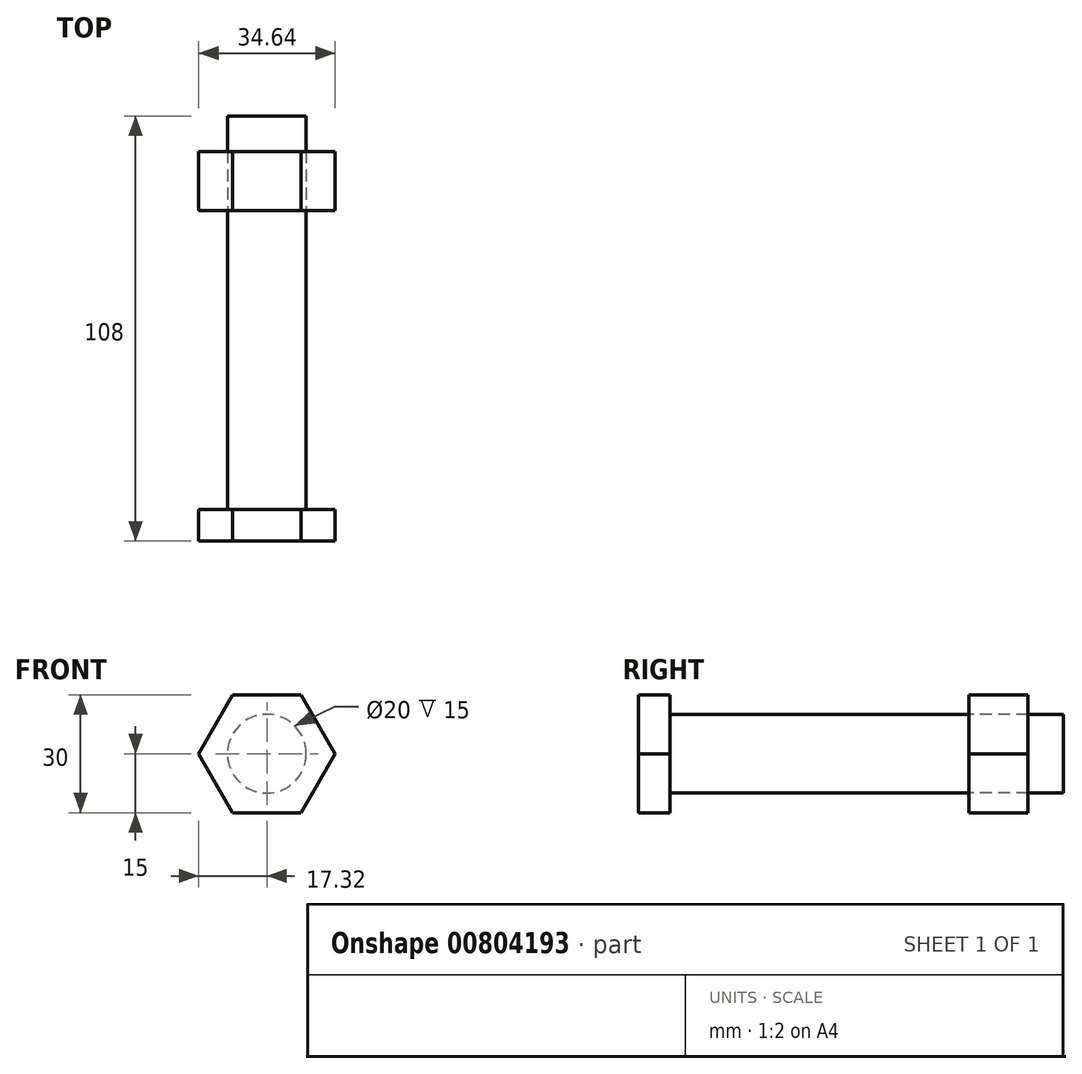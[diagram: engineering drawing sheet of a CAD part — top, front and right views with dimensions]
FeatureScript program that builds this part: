
annotation { "Feature Type Name" : "Feature", "Feature Type Description" : "" }
export const myFeature = defineFeature(function(context is Context, id is Id, definition is map)
    precondition{}
    {
        {
            var Q0;
            Q0=qCreatedBy(makeId("Front.planeOp"),FACE);
            var sketch = newSketch(context, id + "F0", { "sketchPlane" : qUnion([Q0])});
            skCircle(sketch, "E0.cCircle", {"center": v(0, 0) * mm, "radius": 15 * mm, "construction": true});
            skLineSegment(sketch, "E0.0", {"start": v(8.66, 15) * mm, "end": v(17.32, 0) * mm});
            skLineSegment(sketch, "E0.1", {"start": v(17.32, 0) * mm, "end": v(8.66, -15) * mm});
            skLineSegment(sketch, "E0.2", {"start": v(8.66, -15) * mm, "end": v(-8.66, -15) * mm});
            skLineSegment(sketch, "E0.3", {"start": v(-8.66, -15) * mm, "end": v(-17.32, 0) * mm});
            skLineSegment(sketch, "E0.4", {"start": v(-17.32, 0) * mm, "end": v(-8.66, 15) * mm});
            skLineSegment(sketch, "E0.5", {"start": v(-8.66, 15) * mm, "end": v(8.66, 15) * mm});
            skPoint(sketch, "E0.0.midPoint", {"position": v(13, 7.5) * mm});
            skLineSegment(sketch, "E1", {"start": v(0, 0) * mm, "end": v(0, 15) * mm, "construction": true});
            skSolve(sketch);
        }
        {
            var Q0;
            Q0 = qSketchRegion(id + "F0", true);
            extrude(context, id + "F1", {"entities" : qUnion([Q0]), "depth" : 8 * mm, "offsetDistance" : 25 * mm});
        }
        {
            var Q0;
            Q0=makeQuery(id+"F1.opExtrude","CAP_FACE",FACE,{"disambiguationData":[OSD([sQuery(id+"F0.wireOp",EDGE,"E0.0"),sQuery(id+"F0.wireOp",EDGE,"E0.1"),sQuery(id+"F0.wireOp",EDGE,"E0.2"),sQuery(id+"F0.wireOp",EDGE,"E0.3"),sQuery(id+"F0.wireOp",EDGE,"E0.4"),sQuery(id+"F0.wireOp",EDGE,"E0.5")])],"isStart":true});
            var sketch = newSketch(context, id + "F2", { "sketchPlane" : qUnion([Q0])});
            skCircle(sketch, "E2", {"center": v(0, 0) * mm, "radius": 10 * mm});
            skSolve(sketch);
        }
        {
            var Q0;
            Q0 = qSketchRegion(id + "F2", true);
            extrude(context, id + "F3", {"entities" : qUnion([Q0]), "operationType" : NewBodyOperationType.ADD, "depth" : 100 * mm, "offsetDistance" : 25 * mm});
        }
        {
            var Q0;
            Q0=qCreatedBy(makeId("Front.planeOp"),FACE);
            cPlane(context, id + "F4", {"entities" : qUnion([Q0]), "cplaneType" : CPlaneType.OFFSET, "offset" : 76 * mm, "oppositeDirection" : true, "width" : 150 * mm, "height" : 150 * mm});
        }
        {
            var Q0;
            Q0=qCreatedBy(id+"F4.planeOp",FACE);
            var sketch = newSketch(context, id + "F5", { "sketchPlane" : qUnion([Q0])});
            skCircle(sketch, "E3.cCircle", {"center": v(0, 0) * mm, "radius": 15 * mm, "construction": true});
            skLineSegment(sketch, "E3.0", {"start": v(-8.66, -15) * mm, "end": v(-17.32, 0) * mm});
            skLineSegment(sketch, "E3.1", {"start": v(-17.32, 0) * mm, "end": v(-8.66, 15) * mm});
            skLineSegment(sketch, "E3.2", {"start": v(-8.66, 15) * mm, "end": v(8.66, 15) * mm});
            skLineSegment(sketch, "E3.3", {"start": v(8.66, 15) * mm, "end": v(17.32, 0) * mm});
            skLineSegment(sketch, "E3.4", {"start": v(17.32, 0) * mm, "end": v(8.66, -15) * mm});
            skLineSegment(sketch, "E3.5", {"start": v(8.66, -15) * mm, "end": v(-8.66, -15) * mm});
            skPoint(sketch, "E3.0.midPoint", {"position": v(-13, -7.5) * mm});
            skSolve(sketch);
        }
        {
            var Q0;
            Q0=makeQuery(id+"F5.imprint","IMPRINT",FACE,{"disambiguationData":[TD([[makeQuery(id+"F5.imprint","IMPRINT",EDGE,{"derivedFrom":sQuery(id+"F5.wireOp",EDGE,"E3.0")}),-1.0]])]});
            extrude(context, id + "F6", {"entities" : qUnion([Q0]), "oppositeDirection" : true, "depth" : 15 * mm, "offsetDistance" : 25 * mm});
        }
        {
            var Q0;
            Q0=makeQuery(id+"F1.opExtrude","SWEPT_BODY",BODY,{"disambiguationData":[OSD([sQuery(id+"F0.wireOp",EDGE,"E0.0"),sQuery(id+"F0.wireOp",EDGE,"E0.1"),sQuery(id+"F0.wireOp",EDGE,"E0.2"),sQuery(id+"F0.wireOp",EDGE,"E0.3"),sQuery(id+"F0.wireOp",EDGE,"E0.4"),sQuery(id+"F0.wireOp",EDGE,"E0.5")])]});
            var Q1;
            Q1=makeQuery(id+"F6.opExtrude","SWEPT_BODY",BODY,{"disambiguationData":[OSD([sQuery(id+"F5.wireOp",EDGE,"E3.0"),sQuery(id+"F5.wireOp",EDGE,"E3.1"),sQuery(id+"F5.wireOp",EDGE,"E3.2"),sQuery(id+"F5.wireOp",EDGE,"E3.3"),sQuery(id+"F5.wireOp",EDGE,"E3.4"),sQuery(id+"F5.wireOp",EDGE,"E3.5")])]});
            booleanBodies(context, id + "F7", {"operationType" : BooleanOperationType.SUBTRACTION, "tools" : qUnion([Q0]), "targets" : qUnion([Q1]), "keepTools" : true});
        }
    });
